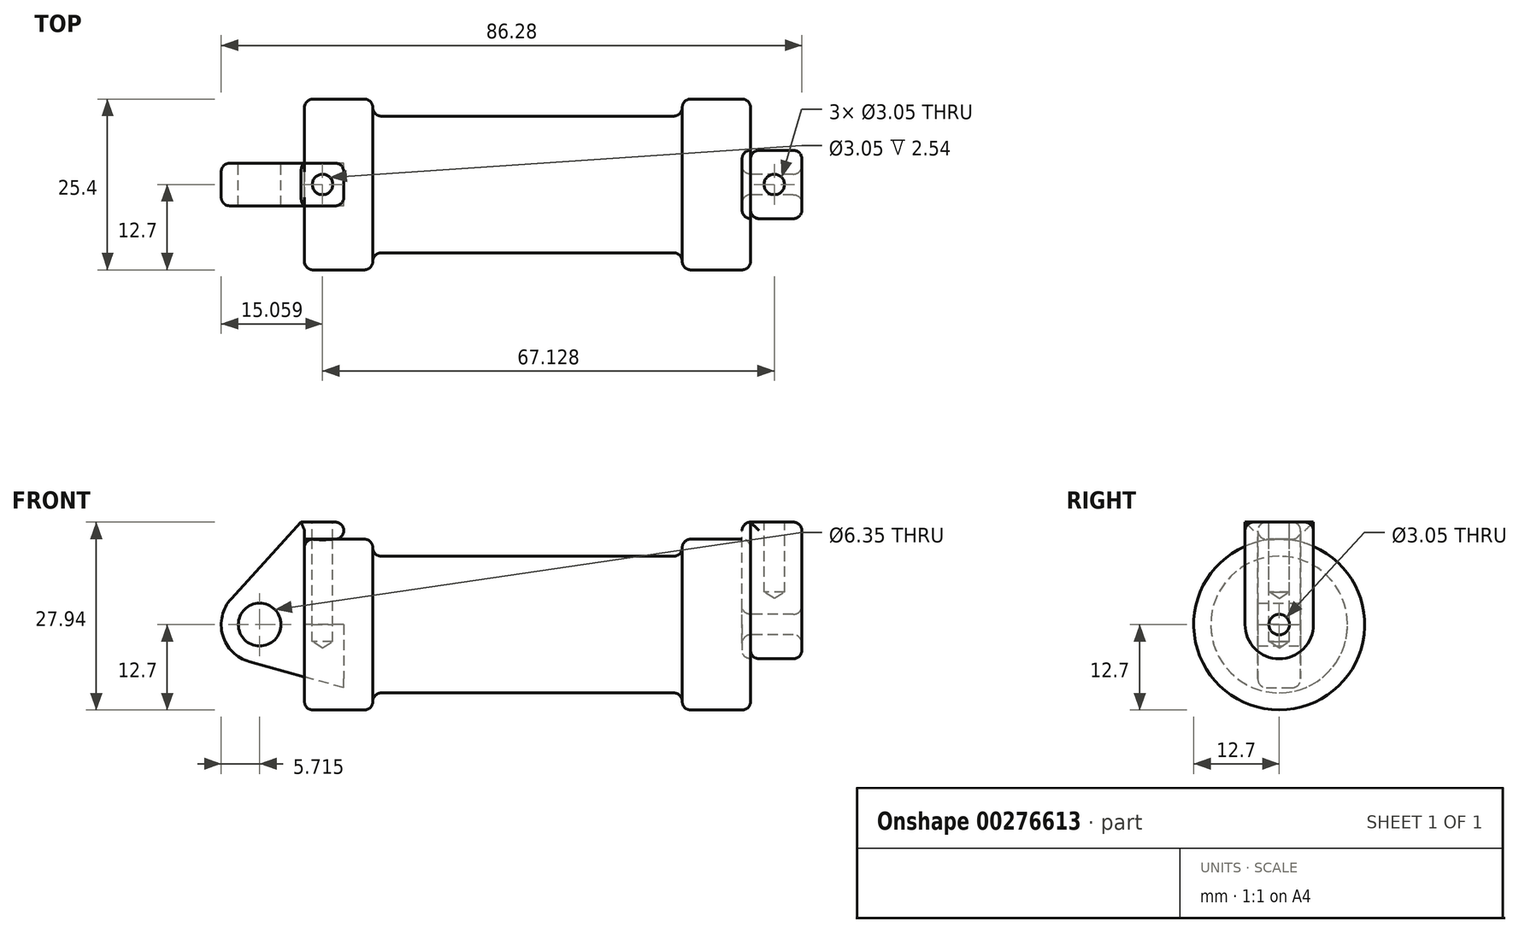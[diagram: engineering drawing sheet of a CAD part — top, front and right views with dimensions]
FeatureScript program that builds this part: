
annotation { "Feature Type Name" : "Feature", "Feature Type Description" : "" }
export const myFeature = defineFeature(function(context is Context, id is Id, definition is map)
    precondition{}
    {
        {
            var Q0;
            Q0=qCreatedBy(makeId("Front.planeOp"),FACE);
            var sketch = newSketch(context, id + "F0", { "sketchPlane" : qUnion([Q0])});
            skLineSegment(sketch, "E0", {"start": v(0, 0) * mm, "end": v(0, 12.7) * mm});
            skLineSegment(sketch, "E1", {"start": v(0, 12.7) * mm, "end": v(10.16, 12.7) * mm});
            skLineSegment(sketch, "E2", {"start": v(10.16, 12.7) * mm, "end": v(10.16, 10.16) * mm});
            skLineSegment(sketch, "E3", {"start": v(10.16, 10.16) * mm, "end": v(56.13, 10.16) * mm});
            skLineSegment(sketch, "E4", {"start": v(56.13, 10.16) * mm, "end": v(56.13, 12.7) * mm});
            skLineSegment(sketch, "E5", {"start": v(56.13, 12.7) * mm, "end": v(66.3, 12.7) * mm});
            skLineSegment(sketch, "E6", {"start": v(66.3, 12.7) * mm, "end": v(66.3, 0) * mm});
            skLineSegment(sketch, "E7", {"start": v(66.3, 0) * mm, "end": v(0, 0) * mm});
            skLineSegment(sketch, "E8", {"start": v(5.84, 15.24) * mm, "end": v(-0.5, 15.24) * mm});
            skLineSegment(sketch, "E9", {"start": v(-0.5, 15.24) * mm, "end": v(-10.88, 3.85) * mm});
            skLineSegment(sketch, "E10", {"start": v(0, 0) * mm, "end": v(-6.65, 0) * mm});
            skCircle(sketch, "E11", {"center": v(-6.65, 0) * mm, "radius": 5.72 * mm});
            skCircle(sketch, "E12", {"center": v(-6.65, 0) * mm, "radius": 3.18 * mm});
            skLineSegment(sketch, "E13", {"start": v(5.84, 15.24) * mm, "end": v(5.84, -9.4) * mm});
            skLineSegment(sketch, "E14", {"start": v(5.84, -9.4) * mm, "end": v(-8.18, -5.5) * mm});
            skSolve(sketch);
        }
        {
            var Q0;
            {var subQ0=sQuery(id+"F0.wireOp",EDGE,"E2");Q0=makeQuery(id+"F0.imprint","IMPRINT",FACE,{"disambiguationData":[TD([[makeQuery(id+"F0.imprint","IMPRINT",EDGE,{"derivedFrom":subQ0}),-1.0]])]});}
            var Q1;
            {var subQ0=sQuery(id+"F0.wireOp",EDGE,"E0");Q1=makeQuery(id+"F0.imprint","IMPRINT",FACE,{"disambiguationData":[TD([[makeQuery(id+"F0.imprint","IMPRINT",EDGE,{"derivedFrom":subQ0}),-1.0]])]});}
            var Q2;
            Q2=sQuery(id+"F0.wireOp",EDGE,"E7");
            revolve(context, id + "F8", {"entities" : qUnion([Q0, Q1]), "axis" : qUnion([Q2]), "revolveType" : RevolveType.FULL});
        }
        {
            var Q0;
            {var subQ0=sQuery(id+"F0.wireOp",EDGE,"E14");Q0=makeQuery(id+"F0.imprint","IMPRINT",FACE,{"disambiguationData":[TD([[makeQuery(id+"F0.imprint","IMPRINT",EDGE,{"derivedFrom":subQ0}),-1.0]])]});}
            var Q1;
            {var subQ3=sQuery(id+"F0.wireOp",EDGE,"E0");Q1=makeQuery(id+"F0.imprint","IMPRINT",FACE,{"disambiguationData":[TD([[makeQuery(id+"F0.imprint","IMPRINT",EDGE,{"derivedFrom":subQ3}),1.0]])]});}
            var Q2;
            {var subQ4=sQuery(id+"F0.wireOp",EDGE,"E12");Q2=makeQuery(id+"F0.imprint","IMPRINT",FACE,{"disambiguationData":[TD([[makeQuery(id+"F0.imprint","IMPRINT",EDGE,{"derivedFrom":subQ4}),-1.0]])]});}
            var Q3;
            Q3=sQuery(id+"F0.wireOp",EDGE,"E7");
            extrude(context, id + "F1", {"entities" : qUnion([Q0, Q1, Q2]), "surfaceEntities" : qUnion([Q3]), "depth" : 3.17 * mm, "hasSecondDirection" : true, "secondDirectionOppositeDirection" : true, "secondDirectionDepth" : 3.17 * mm});
        }
        {
            var Q0;
            Q0=makeQuery(id+"F8.opRevolve","SWEPT_FACE",FACE,{"disambiguationData":[OSD([sQuery(id+"F0.wireOp",EDGE,"E6")])]});
            var sketch = newSketch(context, id + "F2", { "sketchPlane" : qUnion([Q0])});
            skCircle(sketch, "E15", {"center": v(0, 0) * mm, "radius": 5.08 * mm});
            skCircle(sketch, "E16", {"center": v(0, 0) * mm, "radius": 1.52 * mm});
            skLineSegment(sketch, "E17", {"start": v(5.08, 0) * mm, "end": v(5.08, 15.24) * mm});
            skLineSegment(sketch, "E18", {"start": v(-5.08, 0) * mm, "end": v(-5.08, 15.24) * mm});
            skLineSegment(sketch, "E19", {"start": v(-5.08, 15.24) * mm, "end": v(5.08, 15.24) * mm});
            skSolve(sketch);
        }
        {
            var Q0;
            Q0 = qSketchRegion(id + "F2", true);
            extrude(context, id + "F9", {"entities" : qUnion([Q0]), "depth" : 7.62 * mm});
        }
        {
            var Q0;
            Q0=makeQuery(id+"F9.opExtrude","CAP_FACE",FACE,{"disambiguationData":[OSD([sQuery(id+"F2.wireOp",EDGE,"E15"),sQuery(id+"F2.wireOp",EDGE,"E16"),sQuery(id+"F2.wireOp",EDGE,"E17"),sQuery(id+"F2.wireOp",EDGE,"E18"),sQuery(id+"F2.wireOp",EDGE,"E19")])],"isStart":true});
            extrude(context, id + "F10", {"entities" : qUnion([Q0]), "depth" : 1.27 * mm});
        }
        {
            var Q0;
            Q0=makeQuery(id+"F1.opExtrude","SWEPT_FACE",FACE,{"disambiguationData":[OSD([sQuery(id+"F0.wireOp",EDGE,"E8")])]});
            var sketch = newSketch(context, id + "F3", { "sketchPlane" : qUnion([Q0])});
            skCircle(sketch, "E20", {"center": v(69.82, 0) * mm, "radius": 1.52 * mm});
            skPoint(sketch, "E21.center.orphan", {"position": v(2.69, 0) * mm});
            skSolve(sketch);
        }
        {
            var Q0;
            Q0=sQuery(id+"F3.wireOp",VERTEX,"E20.center");
            var Q1;
            Q1=makeQuery(id+"F9.opExtrude","SWEPT_BODY",BODY,{"disambiguationData":[OSD([sQuery(id+"F2.wireOp",EDGE,"E15"),sQuery(id+"F2.wireOp",EDGE,"E16"),sQuery(id+"F2.wireOp",EDGE,"E17"),sQuery(id+"F2.wireOp",EDGE,"E18"),sQuery(id+"F2.wireOp",EDGE,"E19")])]});
            hole(context, id + "F4", {"style" : HoleStyle.SIMPLE, "endStyle" : HoleEndStyle.BLIND, "holeDiameter" : 3.05 * mm, "holeDepth" : 10.4 * mm, "tappedDepth" : 12.7 * mm, "tapClearance" : 3, "locations" : qUnion([Q0]), "scope" : qUnion([Q1])});
        }
        {
            var Q0;
            Q0=sQuery(id+"F3.wireOp",VERTEX,"E21.center.orphan");
            var Q1;
            Q1=makeQuery(id+"F8.opRevolve","SWEPT_BODY",BODY,{"disambiguationData":[OSD([sQuery(id+"F0.wireOp",EDGE,"E0"),sQuery(id+"F0.wireOp",EDGE,"E1"),sQuery(id+"F0.wireOp",EDGE,"E2"),sQuery(id+"F0.wireOp",EDGE,"E3"),sQuery(id+"F0.wireOp",EDGE,"E4"),sQuery(id+"F0.wireOp",EDGE,"E5"),sQuery(id+"F0.wireOp",EDGE,"E6"),sQuery(id+"F0.wireOp",EDGE,"E7")])]});
            var Q2;
            Q2=makeQuery(id+"F1.opExtrude","SWEPT_BODY",BODY,{"disambiguationData":[OSD([sQuery(id+"F0.wireOp",EDGE,"E0"),sQuery(id+"F0.wireOp",EDGE,"E1"),sQuery(id+"F0.wireOp",EDGE,"E7"),sQuery(id+"F0.wireOp",EDGE,"E8"),sQuery(id+"F0.wireOp",EDGE,"E9"),sQuery(id+"F0.wireOp",EDGE,"E11"),sQuery(id+"F0.wireOp",EDGE,"E12"),sQuery(id+"F0.wireOp",EDGE,"E13"),sQuery(id+"F0.wireOp",EDGE,"E14")])]});
            hole(context, id + "F5", {"style" : HoleStyle.SIMPLE, "endStyle" : HoleEndStyle.BLIND, "holeDiameter" : 3.05 * mm, "holeDepth" : 17.78 * mm, "tappedDepth" : 12.7 * mm, "tapClearance" : 3, "locations" : qUnion([Q0]), "scope" : qUnion([Q1, Q2])});
        }
        {
            var Q0;
            Q0=makeQuery(id+"F1.opExtrude","SWEPT_EDGE",EDGE,{"disambiguationData":[OSD([sQuery(id+"F0.wireOp",EDGE,"E1"),sQuery(id+"F0.wireOp",EDGE,"E13")])]});
            var Q1;
            Q1=makeQuery(id+"F1.opExtrude","SWEPT_EDGE",EDGE,{"disambiguationData":[OSD([sQuery(id+"F0.wireOp",EDGE,"E8"),sQuery(id+"F0.wireOp",EDGE,"E13")])]});
            var Q2;
            Q2=makeQuery(id+"F1.opExtrude","CAP_EDGE",EDGE,{"disambiguationData":[OSD([sQuery(id+"F0.wireOp",EDGE,"E1")])],"isStart":false});
            var Q3;
            Q3=makeQuery(id+"F1.opExtrude","CAP_EDGE",EDGE,{"disambiguationData":[OSD([sQuery(id+"F0.wireOp",EDGE,"E8")])],"isStart":false});
            var Q4;
            {var subQ0=sQuery(id+"F0.wireOp",EDGE,"E13");Q4=makeQuery(id+"F1.opExtrude","CAP_EDGE",EDGE,{"disambiguationData":[OSD([subQ0]),TDD([makeQuery(id+"F0.imprint","IMPRINT",EDGE,{"disambiguationData":[TD([[makeQuery(id+"F0.imprint","INTERSECT",VERTEX,{"derivedFrom":[sQuery(id+"F0.wireOp",EDGE,"E8"),subQ0]}),-1.0]])],"derivedFrom":subQ0})])],"isStart":true});}
            var Q5;
            Q5=makeQuery(id+"F1.opExtrude","CAP_EDGE",EDGE,{"disambiguationData":[OSD([sQuery(id+"F0.wireOp",EDGE,"E1")])],"isStart":true});
            var Q6;
            Q6=makeQuery(id+"F1.opExtrude","CAP_EDGE",EDGE,{"disambiguationData":[OSD([sQuery(id+"F0.wireOp",EDGE,"E8")])],"isStart":true});
            var Q7;
            {var subQ0=sQuery(id+"F0.wireOp",EDGE,"E13");Q7=makeQuery(id+"F1.opExtrude","CAP_EDGE",EDGE,{"disambiguationData":[OSD([subQ0]),TDD([makeQuery(id+"F0.imprint","IMPRINT",EDGE,{"disambiguationData":[TD([[makeQuery(id+"F0.imprint","INTERSECT",VERTEX,{"derivedFrom":[sQuery(id+"F0.wireOp",EDGE,"E8"),subQ0]}),-1.0]])],"derivedFrom":subQ0})])],"isStart":false});}
            fillet(context, id + "F6", {"entities" : qUnion([Q0, Q1, Q2, Q3, Q4, Q5, Q6, Q7]), "radius" : 1.27 * mm, "tangentPropagation" : true, "allowEdgeOverflow" : false});
        }
        {
            var Q0;
            Q0=makeQuery(id+"F1.opExtrude","CAP_EDGE",EDGE,{"disambiguationData":[OSD([sQuery(id+"F0.wireOp",EDGE,"E9")])],"isStart":true});
            var Q1;
            Q1=makeQuery(id+"F1.opExtrude","CAP_EDGE",EDGE,{"disambiguationData":[OSD([sQuery(id+"F0.wireOp",EDGE,"E9")])],"isStart":false});
            var Q2;
            Q2=makeQuery(id+"F1.opExtrude","CAP_EDGE",EDGE,{"disambiguationData":[OSD([sQuery(id+"F0.wireOp",EDGE,"E11")])],"isStart":false});
            var Q3;
            Q3=makeQuery(id+"F1.opExtrude","CAP_EDGE",EDGE,{"disambiguationData":[OSD([sQuery(id+"F0.wireOp",EDGE,"E14")])],"isStart":false});
            var Q4;
            Q4=makeQuery(id+"F1.opExtrude","CAP_EDGE",EDGE,{"disambiguationData":[OSD([sQuery(id+"F0.wireOp",EDGE,"E14")])],"isStart":true});
            var Q5;
            Q5=makeQuery(id+"F1.opExtrude","CAP_EDGE",EDGE,{"disambiguationData":[OSD([sQuery(id+"F0.wireOp",EDGE,"E11")])],"isStart":true});
            fillet(context, id + "F11", {"entities" : qUnion([Q0, Q1, Q2, Q3, Q4, Q5]), "radius" : 1.27 * mm, "allowEdgeOverflow" : false});
        }
        {
            var Q0;
            Q0=makeQuery(id+"F8.opRevolve","SWEPT_EDGE",EDGE,{"disambiguationData":[OSD([sQuery(id+"F0.wireOp",EDGE,"E4"),sQuery(id+"F0.wireOp",EDGE,"E5")])]});
            var Q1;
            Q1=makeQuery(id+"F8.opRevolve","SWEPT_EDGE",EDGE,{"disambiguationData":[OSD([sQuery(id+"F0.wireOp",EDGE,"E3"),sQuery(id+"F0.wireOp",EDGE,"E4")])]});
            var Q2;
            Q2=makeQuery(id+"F8.opRevolve","SWEPT_FACE",FACE,{"disambiguationData":[OSD([sQuery(id+"F0.wireOp",EDGE,"E5")])]});
            var Q3;
            Q3=makeQuery(id+"F10.opExtrude","CAP_EDGE",EDGE,{"disambiguationData":[OSD([sQuery(id+"F2.wireOp",EDGE,"E19")])],"isStart":false});
            var Q4;
            Q4=makeQuery(id+"F10.opExtrude","CAP_EDGE",EDGE,{"disambiguationData":[OSD([sQuery(id+"F2.wireOp",EDGE,"E17")])],"isStart":false});
            var Q5;
            Q5=makeQuery(id+"F10.opExtrude","CAP_FACE",FACE,{"disambiguationData":[OSD([sQuery(id+"F2.wireOp",EDGE,"E15"),sQuery(id+"F2.wireOp",EDGE,"E16"),sQuery(id+"F2.wireOp",EDGE,"E17"),sQuery(id+"F2.wireOp",EDGE,"E18"),sQuery(id+"F2.wireOp",EDGE,"E19")])],"isStart":false});
            var Q6;
            Q6=makeQuery(id+"F9.opExtrude","SWEPT_FACE",FACE,{"disambiguationData":[OSD([sQuery(id+"F2.wireOp",EDGE,"E18")])]});
            var Q7;
            Q7=makeQuery(id+"F9.opExtrude","SWEPT_FACE",FACE,{"disambiguationData":[OSD([sQuery(id+"F2.wireOp",EDGE,"E17")])]});
            var Q8;
            Q8=makeQuery(id+"F9.opExtrude","SWEPT_FACE",FACE,{"disambiguationData":[OSD([sQuery(id+"F2.wireOp",EDGE,"E15")])]});
            var Q9;
            Q9=makeQuery(id+"F9.opExtrude","CAP_FACE",FACE,{"disambiguationData":[OSD([sQuery(id+"F2.wireOp",EDGE,"E15"),sQuery(id+"F2.wireOp",EDGE,"E16"),sQuery(id+"F2.wireOp",EDGE,"E17"),sQuery(id+"F2.wireOp",EDGE,"E18"),sQuery(id+"F2.wireOp",EDGE,"E19")])],"isStart":false});
            var Q10;
            Q10=makeQuery(id+"F8.opRevolve","SWEPT_EDGE",EDGE,{"disambiguationData":[OSD([sQuery(id+"F0.wireOp",EDGE,"E0"),sQuery(id+"F0.wireOp",EDGE,"E1")])]});
            var Q11;
            Q11=makeQuery(id+"F8.opRevolve","SWEPT_EDGE",EDGE,{"disambiguationData":[OSD([sQuery(id+"F0.wireOp",EDGE,"E1"),sQuery(id+"F0.wireOp",EDGE,"E2")])]});
            var Q12;
            Q12=makeQuery(id+"F8.opRevolve","SWEPT_EDGE",EDGE,{"disambiguationData":[OSD([sQuery(id+"F0.wireOp",EDGE,"E2"),sQuery(id+"F0.wireOp",EDGE,"E3")])]});
            fillet(context, id + "F7", {"entities" : qUnion([Q0, Q1, Q2, Q3, Q4, Q5, Q6, Q7, Q8, Q9, Q10, Q11, Q12]), "radius" : 1.27 * mm, "allowEdgeOverflow" : false});
        }
    });
